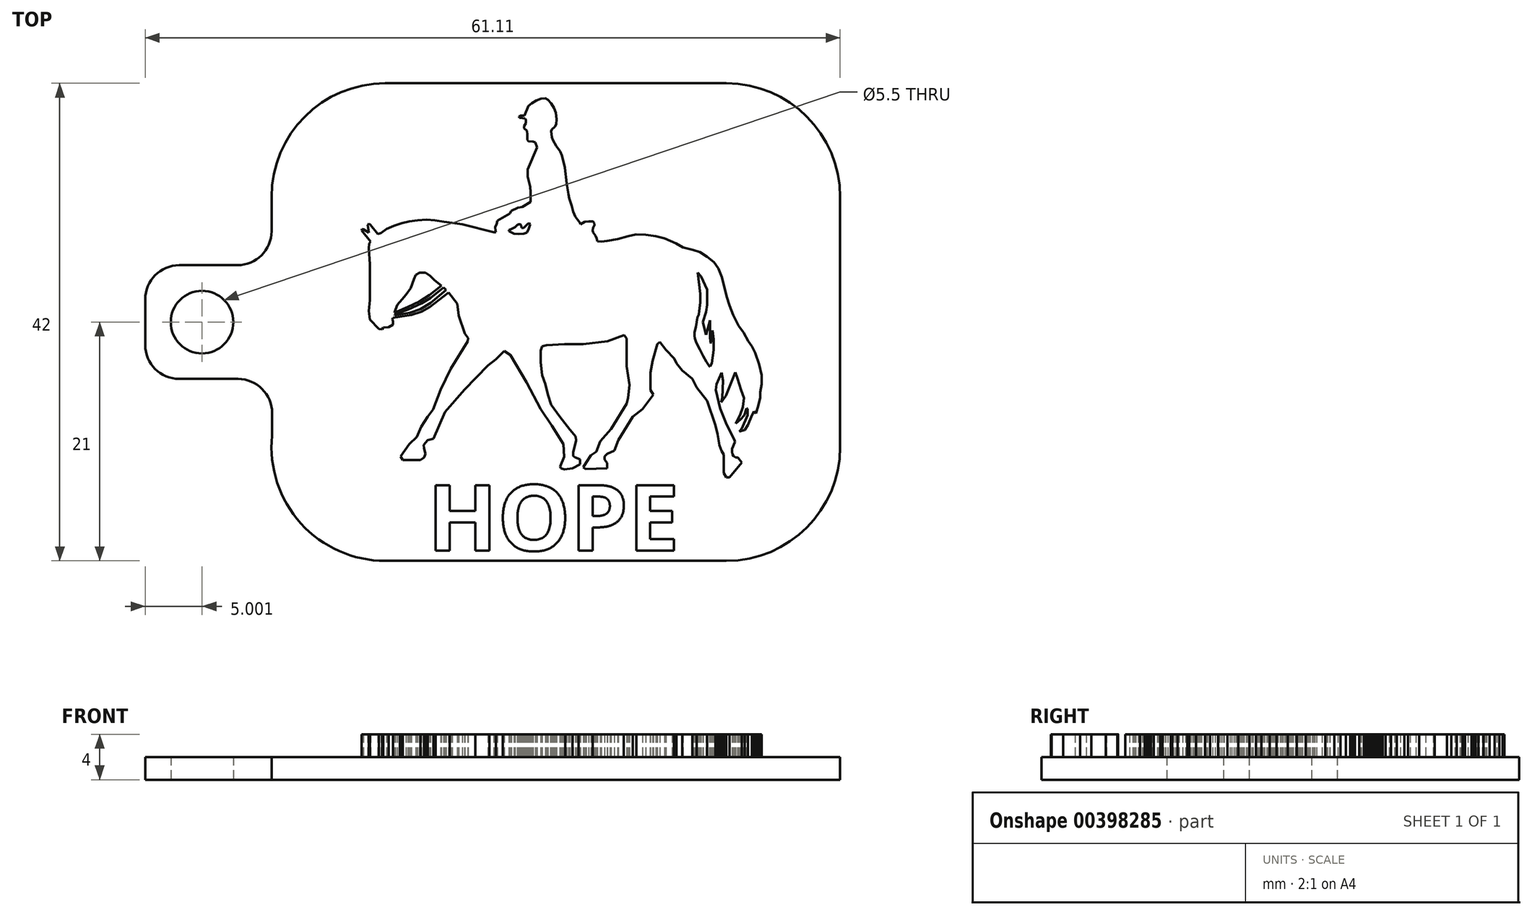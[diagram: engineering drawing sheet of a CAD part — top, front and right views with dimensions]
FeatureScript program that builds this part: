
annotation { "Feature Type Name" : "Feature", "Feature Type Description" : "" }
export const myFeature = defineFeature(function(context is Context, id is Id, definition is map)
    precondition{}
    {
        {
            var Q0;
            Q0=qCreatedBy(makeId("Top.planeOp"),FACE);
            var sketch = newSketch(context, id + "F0", { "sketchPlane" : qUnion([Q0])});
            skLineSegment(sketch, "E0.bottom", {"start": v(-3.2, -21) * mm, "end": v(26.8, -21) * mm});
            skLineSegment(sketch, "E0.top", {"start": v(-3.2, 21) * mm, "end": v(26.8, 21) * mm});
            skLineSegment(sketch, "E0.left", {"start": v(-13.2, 8) * mm, "end": v(-13.2, 11) * mm});
            skLineSegment(sketch, "E0.right", {"start": v(36.8, -11) * mm, "end": v(36.8, 11) * mm});
            skPoint(sketch, "E1.visualSharp", {"position": v(-13.2, 21) * mm});
            skArc(sketch, "E1.filletArc", {"start": v(-3.2, 21) * mm, "mid": v(-10.27, 18.07) * mm, "end": v(-13.2, 11) * mm});
            skPoint(sketch, "E2.visualSharp", {"position": v(36.8, 21) * mm});
            skArc(sketch, "E2.filletArc", {"start": v(36.8, 11) * mm, "mid": v(33.87, 18.07) * mm, "end": v(26.8, 21) * mm});
            skPoint(sketch, "E3.visualSharp", {"position": v(36.8, -21) * mm});
            skArc(sketch, "E3.filletArc", {"start": v(26.8, -21) * mm, "mid": v(33.87, -18.07) * mm, "end": v(36.8, -11) * mm});
            skPoint(sketch, "E4.visualSharp", {"position": v(-13.2, -21) * mm});
            skArc(sketch, "E4.filletArc", {"start": v(-13.15, -10) * mm, "mid": v(-10.62, -17.7) * mm, "end": v(-3.2, -21) * mm});
            skPoint(sketch, "E5.endSnap0", {"position": v(-13.2, 0) * mm});
            skLineSegment(sketch, "E6.0", {"start": v(-16.2, 5) * mm, "end": v(-21.3, 5) * mm});
            skLineSegment(sketch, "E7.0", {"start": v(-16.15, -5) * mm, "end": v(-21.3, -5) * mm});
            skLineSegment(sketch, "E8", {"start": v(-24.3, 2) * mm, "end": v(-24.3, -2) * mm});
            skPoint(sketch, "E9.visualSharp", {"position": v(-24.3, 5) * mm});
            skArc(sketch, "E9.filletArc", {"start": v(-21.3, 5) * mm, "mid": v(-23.43, 4.12) * mm, "end": v(-24.3, 2) * mm});
            skPoint(sketch, "E10.visualSharp", {"position": v(-24.3, -5) * mm});
            skArc(sketch, "E10.filletArc", {"start": v(-24.3, -2) * mm, "mid": v(-23.43, -4.12) * mm, "end": v(-21.3, -5) * mm});
            skPoint(sketch, "E11.centerSnap0", {"position": v(-24.3, 0) * mm});
            skPoint(sketch, "E12.newPointB", {"position": v(-13.2, -11) * mm});
            skArc(sketch, "E12.filletArc", {"start": v(-16.2, 5) * mm, "mid": v(-14.08, 5.88) * mm, "end": v(-13.2, 8) * mm});
            skLineSegment(sketch, "E13", {"start": v(-13.15, -10) * mm, "end": v(-13.15, -8) * mm});
            skPoint(sketch, "E14.visualSharp", {"position": v(-13.15, -5) * mm});
            skArc(sketch, "E14.filletArc", {"start": v(-13.15, -8) * mm, "mid": v(-14.03, -5.88) * mm, "end": v(-16.15, -5) * mm});
            skCircle(sketch, "E15", {"center": v(-19.3, 0) * mm, "radius": 2.75 * mm});
            skSolve(sketch);
        }
        {
            var Q0;
            Q0=makeQuery(id+"F0.imprint","IMPRINT",FACE,{"disambiguationData":[TD([[makeQuery(id+"F0.imprint","IMPRINT",EDGE,{"derivedFrom":sQuery(id+"F0.wireOp",EDGE,"E0.bottom")}),1.0]])]});
            extrude(context, id + "F1", {"entities" : qUnion([Q0]), "depth" : 2 * mm});
        }
        {
            var Q0;
            Q0=makeQuery(id+"F1.opExtrude","CAP_FACE",FACE,{"disambiguationData":[OSD([sQuery(id+"F0.wireOp",EDGE,"E0.bottom"),sQuery(id+"F0.wireOp",EDGE,"E0.top"),sQuery(id+"F0.wireOp",EDGE,"E0.left"),sQuery(id+"F0.wireOp",EDGE,"E0.right"),sQuery(id+"F0.wireOp",EDGE,"E1.filletArc"),sQuery(id+"F0.wireOp",EDGE,"E2.filletArc"),sQuery(id+"F0.wireOp",EDGE,"E3.filletArc"),sQuery(id+"F0.wireOp",EDGE,"E4.filletArc"),sQuery(id+"F0.wireOp",EDGE,"E6.0"),sQuery(id+"F0.wireOp",EDGE,"E7.0"),sQuery(id+"F0.wireOp",EDGE,"E8"),sQuery(id+"F0.wireOp",EDGE,"E9.filletArc"),sQuery(id+"F0.wireOp",EDGE,"E10.filletArc"),sQuery(id+"F0.wireOp",EDGE,"E12.filletArc"),sQuery(id+"F0.wireOp",EDGE,"E13"),sQuery(id+"F0.wireOp",EDGE,"E14.filletArc"),sQuery(id+"F0.wireOp",EDGE,"E15")])],"isStart":false});
            var sketch = newSketch(context, id + "F2", { "sketchPlane" : qUnion([Q0])});
            skLineSegment(sketch, "E16", {"start": v(16.3, -12.87) * mm, "end": v(14.4, -12.93) * mm});
            skLineSegment(sketch, "E17", {"start": v(14.4, -12.93) * mm, "end": v(14.2, -12.76) * mm});
            skLineSegment(sketch, "E18", {"start": v(14.2, -12.76) * mm, "end": v(14.47, -12.34) * mm});
            skLineSegment(sketch, "E19", {"start": v(14.47, -12.34) * mm, "end": v(14.89, -11.72) * mm});
            skLineSegment(sketch, "E20", {"start": v(14.89, -11.72) * mm, "end": v(15.37, -11.4) * mm});
            skLineSegment(sketch, "E21", {"start": v(15.37, -11.4) * mm, "end": v(15.72, -10.49) * mm});
            skLineSegment(sketch, "E22", {"start": v(15.72, -10.49) * mm, "end": v(16.66, -9.4) * mm});
            skLineSegment(sketch, "E23", {"start": v(16.66, -9.4) * mm, "end": v(18.04, -7.18) * mm});
            skLineSegment(sketch, "E24", {"start": v(18.04, -7.18) * mm, "end": v(18.15, -6.68) * mm});
            skLineSegment(sketch, "E25", {"start": v(18.15, -6.68) * mm, "end": v(18.28, -5.52) * mm});
            skLineSegment(sketch, "E26", {"start": v(18.28, -5.52) * mm, "end": v(18.04, -3.88) * mm});
            skLineSegment(sketch, "E27", {"start": v(18.04, -3.88) * mm, "end": v(18.04, -2.46) * mm});
            skLineSegment(sketch, "E28", {"start": v(18.04, -2.46) * mm, "end": v(18.04, -1.42) * mm});
            skLineSegment(sketch, "E29", {"start": v(18.04, -1.42) * mm, "end": v(17.82, -1.14) * mm});
            skLineSegment(sketch, "E30", {"start": v(17.82, -1.14) * mm, "end": v(16.33, -1.68) * mm});
            skLineSegment(sketch, "E31", {"start": v(16.33, -1.68) * mm, "end": v(14.22, -1.94) * mm});
            skLineSegment(sketch, "E32", {"start": v(14.22, -1.94) * mm, "end": v(12.55, -1.94) * mm});
            skLineSegment(sketch, "E33", {"start": v(12.55, -1.94) * mm, "end": v(10.97, -2.03) * mm});
            skLineSegment(sketch, "E34", {"start": v(10.97, -2.03) * mm, "end": v(10.59, -2.12) * mm});
            skLineSegment(sketch, "E35", {"start": v(10.59, -2.12) * mm, "end": v(10.47, -2.52) * mm});
            skLineSegment(sketch, "E36", {"start": v(10.47, -2.52) * mm, "end": v(10.47, -3.52) * mm});
            skLineSegment(sketch, "E37", {"start": v(10.47, -3.52) * mm, "end": v(10.6, -4.66) * mm});
            skLineSegment(sketch, "E38", {"start": v(10.6, -4.66) * mm, "end": v(10.88, -5.47) * mm});
            skLineSegment(sketch, "E39", {"start": v(10.88, -5.47) * mm, "end": v(11.1, -6.4) * mm});
            skLineSegment(sketch, "E40", {"start": v(11.1, -6.4) * mm, "end": v(11.39, -7.28) * mm});
            skLineSegment(sketch, "E41", {"start": v(11.39, -7.28) * mm, "end": v(12.15, -8.34) * mm});
            skLineSegment(sketch, "E42", {"start": v(12.15, -8.34) * mm, "end": v(13.04, -9.48) * mm});
            skLineSegment(sketch, "E43", {"start": v(13.04, -9.48) * mm, "end": v(13.55, -10.07) * mm});
            skLineSegment(sketch, "E44", {"start": v(13.55, -10.07) * mm, "end": v(13.6, -10.4) * mm});
            skLineSegment(sketch, "E45", {"start": v(13.6, -10.4) * mm, "end": v(13.33, -11.45) * mm});
            skLineSegment(sketch, "E46", {"start": v(13.33, -11.45) * mm, "end": v(13.33, -11.77) * mm});
            skLineSegment(sketch, "E47", {"start": v(13.33, -11.77) * mm, "end": v(13.52, -11.9) * mm});
            skLineSegment(sketch, "E48", {"start": v(13.52, -11.9) * mm, "end": v(13.92, -12.07) * mm});
            skLineSegment(sketch, "E49", {"start": v(13.92, -12.07) * mm, "end": v(13.92, -12.5) * mm});
            skLineSegment(sketch, "E50", {"start": v(13.92, -12.5) * mm, "end": v(13.27, -12.88) * mm});
            skLineSegment(sketch, "E51", {"start": v(13.27, -12.88) * mm, "end": v(12.55, -12.97) * mm});
            skLineSegment(sketch, "E52", {"start": v(12.55, -12.97) * mm, "end": v(12.25, -12.88) * mm});
            skLineSegment(sketch, "E53", {"start": v(12.25, -12.88) * mm, "end": v(12.19, -12.7) * mm});
            skLineSegment(sketch, "E54", {"start": v(12.19, -12.7) * mm, "end": v(12.54, -11.84) * mm});
            skLineSegment(sketch, "E55", {"start": v(12.54, -11.84) * mm, "end": v(12.46, -10.72) * mm});
            skLineSegment(sketch, "E56", {"start": v(12.46, -10.72) * mm, "end": v(11.44, -9.1) * mm});
            skLineSegment(sketch, "E57", {"start": v(11.44, -9.1) * mm, "end": v(10.47, -7.66) * mm});
            skLineSegment(sketch, "E58", {"start": v(10.47, -7.66) * mm, "end": v(9.22, -5.32) * mm});
            skLineSegment(sketch, "E59", {"start": v(9.22, -5.32) * mm, "end": v(7.82, -2.88) * mm});
            skLineSegment(sketch, "E60", {"start": v(7.82, -2.88) * mm, "end": v(7.25, -2.53) * mm});
            skLineSegment(sketch, "E61", {"start": v(7.25, -2.53) * mm, "end": v(6.53, -3.27) * mm});
            skLineSegment(sketch, "E62", {"start": v(6.53, -3.27) * mm, "end": v(5.84, -3.81) * mm});
            skLineSegment(sketch, "E63", {"start": v(5.84, -3.81) * mm, "end": v(3.76, -5.94) * mm});
            skLineSegment(sketch, "E64", {"start": v(3.76, -5.94) * mm, "end": v(2.06, -7.9) * mm});
            skLineSegment(sketch, "E65", {"start": v(2.06, -7.9) * mm, "end": v(1.04, -10.26) * mm});
            skLineSegment(sketch, "E66", {"start": v(1.04, -10.26) * mm, "end": v(0.54, -10.38) * mm});
            skLineSegment(sketch, "E67", {"start": v(0.54, -10.38) * mm, "end": v(0.19, -10.8) * mm});
            skLineSegment(sketch, "E68", {"start": v(0.19, -10.8) * mm, "end": v(0.23, -11.13) * mm});
            skLineSegment(sketch, "E69", {"start": v(0.23, -11.13) * mm, "end": v(0.34, -11.6) * mm});
            skLineSegment(sketch, "E70", {"start": v(0.34, -11.6) * mm, "end": v(0.2, -11.9) * mm});
            skLineSegment(sketch, "E71", {"start": v(0.2, -11.9) * mm, "end": v(-0.1, -12.14) * mm});
            skLineSegment(sketch, "E72", {"start": v(-0.1, -12.14) * mm, "end": v(-1.65, -12.14) * mm});
            skLineSegment(sketch, "E73", {"start": v(-1.65, -12.14) * mm, "end": v(-1.85, -11.8) * mm});
            skLineSegment(sketch, "E74", {"start": v(-1.85, -11.8) * mm, "end": v(-1.1, -10.72) * mm});
            skLineSegment(sketch, "E75", {"start": v(-1.1, -10.72) * mm, "end": v(-0.43, -10.1) * mm});
            skLineSegment(sketch, "E76", {"start": v(-0.43, -10.1) * mm, "end": v(-0.05, -9.22) * mm});
            skLineSegment(sketch, "E77", {"start": v(-0.05, -9.22) * mm, "end": v(0.54, -8.34) * mm});
            skLineSegment(sketch, "E78", {"start": v(0.54, -8.34) * mm, "end": v(1, -7.7) * mm});
            skLineSegment(sketch, "E79", {"start": v(1, -7.7) * mm, "end": v(1.68, -5.95) * mm});
            skLineSegment(sketch, "E80", {"start": v(1.68, -5.95) * mm, "end": v(2.57, -4.1) * mm});
            skLineSegment(sketch, "E81", {"start": v(2.57, -4.1) * mm, "end": v(4.06, -1.68) * mm});
            skLineSegment(sketch, "E82", {"start": v(4.06, -1.68) * mm, "end": v(4.1, -1.4) * mm});
            skLineSegment(sketch, "E83", {"start": v(4.1, -1.4) * mm, "end": v(3.8, -1.01) * mm});
            skLineSegment(sketch, "E84", {"start": v(3.8, -1.01) * mm, "end": v(3.26, 0.58) * mm});
            skLineSegment(sketch, "E85", {"start": v(3.26, 0.58) * mm, "end": v(3.13, 1.63) * mm});
            skLineSegment(sketch, "E86", {"start": v(3.13, 1.63) * mm, "end": v(2.36, 2.6) * mm});
            skLineSegment(sketch, "E87", {"start": v(2.36, 2.6) * mm, "end": v(0.71, 1.32) * mm});
            skLineSegment(sketch, "E88", {"start": v(0.71, 1.32) * mm, "end": v(0, 0.9) * mm});
            skLineSegment(sketch, "E89", {"start": v(0, 0.9) * mm, "end": v(-0.9, 0.65) * mm});
            skLineSegment(sketch, "E90", {"start": v(-0.9, 0.65) * mm, "end": v(-1.91, 0.46) * mm});
            skLineSegment(sketch, "E91", {"start": v(-1.91, 0.46) * mm, "end": v(-2.5, 0.39) * mm});
            skLineSegment(sketch, "E92", {"start": v(-2.5, 0.39) * mm, "end": v(-2.58, 0.23) * mm});
            skLineSegment(sketch, "E93", {"start": v(-2.58, 0.23) * mm, "end": v(-2.53, 0.1) * mm});
            skLineSegment(sketch, "E94", {"start": v(-2.53, 0.1) * mm, "end": v(-2.5, 0) * mm});
            skLineSegment(sketch, "E95", {"start": v(-2.5, 0) * mm, "end": v(-2.5, -0.21) * mm});
            skLineSegment(sketch, "E96", {"start": v(-2.5, -0.21) * mm, "end": v(-2.89, -0.43) * mm});
            skLineSegment(sketch, "E97", {"start": v(-2.89, -0.43) * mm, "end": v(-3.4, -0.5) * mm});
            skLineSegment(sketch, "E98", {"start": v(-3.4, -0.5) * mm, "end": v(-3.47, -0.63) * mm});
            skLineSegment(sketch, "E99", {"start": v(-3.47, -0.63) * mm, "end": v(-3.75, -0.6) * mm});
            skLineSegment(sketch, "E100", {"start": v(-3.75, -0.6) * mm, "end": v(-4.56, 0.22) * mm});
            skLineSegment(sketch, "E101", {"start": v(-4.56, 0.22) * mm, "end": v(-4.66, 1) * mm});
            skLineSegment(sketch, "E102", {"start": v(-4.66, 1) * mm, "end": v(-4.55, 1.94) * mm});
            skLineSegment(sketch, "E103", {"start": v(-4.55, 1.94) * mm, "end": v(-4.55, 3.1) * mm});
            skLineSegment(sketch, "E104", {"start": v(-4.55, 3.1) * mm, "end": v(-4.55, 5.06) * mm});
            skLineSegment(sketch, "E105", {"start": v(-4.55, 5.06) * mm, "end": v(-4.66, 6.47) * mm});
            skLineSegment(sketch, "E106", {"start": v(-4.66, 6.47) * mm, "end": v(-4.6, 6.9) * mm});
            skLineSegment(sketch, "E107", {"start": v(-4.6, 6.9) * mm, "end": v(-4.5, 7.08) * mm});
            skLineSegment(sketch, "E108", {"start": v(-4.5, 7.08) * mm, "end": v(-4.95, 7.66) * mm});
            skLineSegment(sketch, "E109", {"start": v(-4.95, 7.66) * mm, "end": v(-5.27, 8.07) * mm});
            skLineSegment(sketch, "E110", {"start": v(-5.27, 8.07) * mm, "end": v(-5.25, 8.17) * mm});
            skLineSegment(sketch, "E111", {"start": v(-5.25, 8.17) * mm, "end": v(-5.1, 8.16) * mm});
            skLineSegment(sketch, "E112", {"start": v(-5.1, 8.16) * mm, "end": v(-4.66, 7.88) * mm});
            skLineSegment(sketch, "E113", {"start": v(-4.66, 7.88) * mm, "end": v(-4.74, 8.53) * mm});
            skLineSegment(sketch, "E114", {"start": v(-4.74, 8.53) * mm, "end": v(-4.66, 8.67) * mm});
            skLineSegment(sketch, "E115", {"start": v(-4.66, 8.67) * mm, "end": v(-4.51, 8.58) * mm});
            skLineSegment(sketch, "E116", {"start": v(-4.51, 8.58) * mm, "end": v(-3.85, 7.74) * mm});
            skLineSegment(sketch, "E117", {"start": v(-3.85, 7.74) * mm, "end": v(-3.55, 7.84) * mm});
            skLineSegment(sketch, "E118", {"start": v(-3.55, 7.84) * mm, "end": v(-3.08, 8.17) * mm});
            skLineSegment(sketch, "E119", {"start": v(-3.08, 8.17) * mm, "end": v(-2.43, 8.47) * mm});
            skLineSegment(sketch, "E120", {"start": v(-2.43, 8.47) * mm, "end": v(-1.76, 8.7) * mm});
            skLineSegment(sketch, "E121", {"start": v(-1.76, 8.7) * mm, "end": v(-1.08, 8.85) * mm});
            skLineSegment(sketch, "E122", {"start": v(-1.08, 8.85) * mm, "end": v(-0.36, 8.94) * mm});
            skLineSegment(sketch, "E123", {"start": v(-0.36, 8.94) * mm, "end": v(0.44, 9) * mm});
            skLineSegment(sketch, "E124", {"start": v(0.44, 9) * mm, "end": v(1.15, 8.95) * mm});
            skLineSegment(sketch, "E125", {"start": v(1.15, 8.95) * mm, "end": v(1.95, 8.82) * mm});
            skLineSegment(sketch, "E126", {"start": v(1.95, 8.82) * mm, "end": v(2.68, 8.74) * mm});
            skLineSegment(sketch, "E127", {"start": v(2.68, 8.74) * mm, "end": v(3.57, 8.6) * mm});
            skLineSegment(sketch, "E128", {"start": v(3.57, 8.6) * mm, "end": v(4.4, 8.4) * mm});
            skLineSegment(sketch, "E129", {"start": v(4.4, 8.4) * mm, "end": v(5.28, 8.17) * mm});
            skLineSegment(sketch, "E130", {"start": v(5.28, 8.17) * mm, "end": v(6.34, 7.91) * mm});
            skLineSegment(sketch, "E131", {"start": v(6.34, 7.91) * mm, "end": v(6.53, 7.89) * mm});
            skLineSegment(sketch, "E132", {"start": v(6.53, 7.89) * mm, "end": v(6.5, 8) * mm});
            skLineSegment(sketch, "E133", {"start": v(6.5, 8) * mm, "end": v(6.45, 8.38) * mm});
            skLineSegment(sketch, "E134", {"start": v(6.45, 8.38) * mm, "end": v(6.59, 8.6) * mm});
            skLineSegment(sketch, "E135", {"start": v(6.59, 8.6) * mm, "end": v(6.67, 8.93) * mm});
            skLineSegment(sketch, "E136", {"start": v(6.67, 8.93) * mm, "end": v(7.17, 9.22) * mm});
            skLineSegment(sketch, "E137", {"start": v(7.17, 9.22) * mm, "end": v(7.77, 9.57) * mm});
            skLineSegment(sketch, "E138", {"start": v(7.77, 9.57) * mm, "end": v(7.86, 9.78) * mm});
            skLineSegment(sketch, "E139", {"start": v(7.86, 9.78) * mm, "end": v(8.47, 10.05) * mm});
            skLineSegment(sketch, "E140", {"start": v(8.47, 10.05) * mm, "end": v(8.84, 10.13) * mm});
            skLineSegment(sketch, "E141", {"start": v(8.84, 10.13) * mm, "end": v(9.6, 10.57) * mm});
            skLineSegment(sketch, "E142", {"start": v(9.6, 10.57) * mm, "end": v(9.6, 11.1) * mm});
            skLineSegment(sketch, "E143", {"start": v(9.6, 11.1) * mm, "end": v(9.6, 11.41) * mm});
            skLineSegment(sketch, "E144", {"start": v(9.6, 11.41) * mm, "end": v(9.53, 11.92) * mm});
            skLineSegment(sketch, "E145", {"start": v(9.53, 11.92) * mm, "end": v(9.33, 12.78) * mm});
            skLineSegment(sketch, "E146", {"start": v(9.33, 12.78) * mm, "end": v(9.33, 13.43) * mm});
            skLineSegment(sketch, "E147", {"start": v(9.33, 13.43) * mm, "end": v(9.92, 14.8) * mm});
            skLineSegment(sketch, "E148", {"start": v(9.92, 14.8) * mm, "end": v(10.16, 15.35) * mm});
            skLineSegment(sketch, "E149", {"start": v(10.16, 15.35) * mm, "end": v(9.98, 15.8) * mm});
            skLineSegment(sketch, "E150", {"start": v(9.98, 15.8) * mm, "end": v(9.81, 15.87) * mm});
            skLineSegment(sketch, "E151", {"start": v(9.81, 15.87) * mm, "end": v(9.4, 15.92) * mm});
            skLineSegment(sketch, "E152", {"start": v(9.4, 15.92) * mm, "end": v(9.3, 16.04) * mm});
            skLineSegment(sketch, "E153", {"start": v(9.3, 16.04) * mm, "end": v(9.3, 16.5) * mm});
            skLineSegment(sketch, "E154", {"start": v(9.3, 16.5) * mm, "end": v(9.25, 16.83) * mm});
            skLineSegment(sketch, "E155", {"start": v(9.25, 16.83) * mm, "end": v(9.02, 17.04) * mm});
            skLineSegment(sketch, "E156", {"start": v(9.02, 17.04) * mm, "end": v(9, 17.1) * mm});
            skLineSegment(sketch, "E157", {"start": v(9, 17.1) * mm, "end": v(9, 17.22) * mm});
            skLineSegment(sketch, "E158", {"start": v(9, 17.22) * mm, "end": v(9.17, 17.49) * mm});
            skLineSegment(sketch, "E159", {"start": v(9.17, 17.49) * mm, "end": v(9.17, 17.77) * mm});
            skLineSegment(sketch, "E160", {"start": v(9.17, 17.77) * mm, "end": v(9.12, 17.9) * mm});
            skLineSegment(sketch, "E161", {"start": v(9.12, 17.9) * mm, "end": v(8.88, 17.93) * mm});
            skLineSegment(sketch, "E162", {"start": v(8.88, 17.93) * mm, "end": v(8.6, 17.97) * mm});
            skLineSegment(sketch, "E163", {"start": v(8.6, 17.97) * mm, "end": v(8.58, 18.1) * mm});
            skLineSegment(sketch, "E164", {"start": v(8.58, 18.1) * mm, "end": v(8.67, 18.16) * mm});
            skLineSegment(sketch, "E165", {"start": v(8.67, 18.16) * mm, "end": v(9.03, 18.16) * mm});
            skLineSegment(sketch, "E166", {"start": v(9.03, 18.16) * mm, "end": v(9.4, 19.02) * mm});
            skLineSegment(sketch, "E167", {"start": v(9.4, 19.02) * mm, "end": v(9.69, 19.24) * mm});
            skLineSegment(sketch, "E168", {"start": v(9.69, 19.24) * mm, "end": v(10.1, 19.48) * mm});
            skLineSegment(sketch, "E169", {"start": v(10.1, 19.48) * mm, "end": v(10.5, 19.64) * mm});
            skLineSegment(sketch, "E170", {"start": v(10.5, 19.64) * mm, "end": v(10.88, 19.69) * mm});
            skLineSegment(sketch, "E171", {"start": v(10.88, 19.69) * mm, "end": v(11.1, 19.55) * mm});
            skLineSegment(sketch, "E172", {"start": v(11.1, 19.55) * mm, "end": v(11.39, 19.25) * mm});
            skLineSegment(sketch, "E173", {"start": v(11.39, 19.25) * mm, "end": v(11.63, 18.83) * mm});
            skLineSegment(sketch, "E174", {"start": v(11.63, 18.83) * mm, "end": v(11.8, 18.4) * mm});
            skLineSegment(sketch, "E175", {"start": v(11.8, 18.4) * mm, "end": v(11.87, 17.85) * mm});
            skLineSegment(sketch, "E176", {"start": v(11.87, 17.85) * mm, "end": v(11.82, 17.4) * mm});
            skLineSegment(sketch, "E177", {"start": v(11.82, 17.4) * mm, "end": v(11.72, 17.17) * mm});
            skLineSegment(sketch, "E178", {"start": v(11.72, 17.17) * mm, "end": v(11.46, 16.97) * mm});
            skLineSegment(sketch, "E179", {"start": v(11.46, 16.97) * mm, "end": v(11.39, 16.8) * mm});
            skLineSegment(sketch, "E180", {"start": v(11.39, 16.8) * mm, "end": v(11.4, 16.67) * mm});
            skLineSegment(sketch, "E181", {"start": v(11.4, 16.67) * mm, "end": v(11.43, 16.45) * mm});
            skLineSegment(sketch, "E182", {"start": v(11.43, 16.45) * mm, "end": v(11.46, 16.24) * mm});
            skLineSegment(sketch, "E183", {"start": v(11.46, 16.24) * mm, "end": v(11.55, 16) * mm});
            skLineSegment(sketch, "E184", {"start": v(11.55, 16) * mm, "end": v(11.84, 15.5) * mm});
            skLineSegment(sketch, "E185", {"start": v(11.84, 15.5) * mm, "end": v(12.18, 15.02) * mm});
            skLineSegment(sketch, "E186", {"start": v(12.18, 15.02) * mm, "end": v(12.34, 14.64) * mm});
            skLineSegment(sketch, "E187", {"start": v(12.34, 14.64) * mm, "end": v(12.46, 14.1) * mm});
            skLineSegment(sketch, "E188", {"start": v(12.46, 14.1) * mm, "end": v(12.58, 13.57) * mm});
            skLineSegment(sketch, "E189", {"start": v(12.58, 13.57) * mm, "end": v(12.64, 13.13) * mm});
            skLineSegment(sketch, "E190", {"start": v(12.64, 13.13) * mm, "end": v(12.7, 12.66) * mm});
            skLineSegment(sketch, "E191", {"start": v(12.7, 12.66) * mm, "end": v(12.75, 12.2) * mm});
            skLineSegment(sketch, "E192", {"start": v(12.75, 12.2) * mm, "end": v(12.92, 11.22) * mm});
            skLineSegment(sketch, "E193", {"start": v(12.92, 11.22) * mm, "end": v(12.96, 10.9) * mm});
            skLineSegment(sketch, "E194", {"start": v(12.96, 10.9) * mm, "end": v(13.19, 10.22) * mm});
            skLineSegment(sketch, "E195", {"start": v(13.19, 10.22) * mm, "end": v(13.33, 9.73) * mm});
            skLineSegment(sketch, "E196", {"start": v(13.33, 9.73) * mm, "end": v(13.52, 9.26) * mm});
            skLineSegment(sketch, "E197", {"start": v(13.52, 9.26) * mm, "end": v(13.72, 9) * mm});
            skLineSegment(sketch, "E198", {"start": v(13.72, 9) * mm, "end": v(13.92, 8.73) * mm});
            skLineSegment(sketch, "E199", {"start": v(13.92, 8.73) * mm, "end": v(13.96, 8.61) * mm});
            skLineSegment(sketch, "E200", {"start": v(13.96, 8.61) * mm, "end": v(14.35, 8.8) * mm});
            skLineSegment(sketch, "E201", {"start": v(14.35, 8.8) * mm, "end": v(14.68, 8.85) * mm});
            skLineSegment(sketch, "E202", {"start": v(14.68, 8.85) * mm, "end": v(15.06, 8.85) * mm});
            skLineSegment(sketch, "E203", {"start": v(15.06, 8.85) * mm, "end": v(15.16, 8.73) * mm});
            skLineSegment(sketch, "E204", {"start": v(15.16, 8.73) * mm, "end": v(15.19, 8.54) * mm});
            skLineSegment(sketch, "E205", {"start": v(15.19, 8.54) * mm, "end": v(15.09, 8.3) * mm});
            skLineSegment(sketch, "E206", {"start": v(15.09, 8.3) * mm, "end": v(15.03, 8.07) * mm});
            skLineSegment(sketch, "E207", {"start": v(15.03, 8.07) * mm, "end": v(15.08, 7.89) * mm});
            skLineSegment(sketch, "E208", {"start": v(15.08, 7.89) * mm, "end": v(15.29, 7.6) * mm});
            skLineSegment(sketch, "E209", {"start": v(15.29, 7.6) * mm, "end": v(15.38, 7.38) * mm});
            skLineSegment(sketch, "E210", {"start": v(15.38, 7.38) * mm, "end": v(15.45, 7.12) * mm});
            skLineSegment(sketch, "E211", {"start": v(15.45, 7.12) * mm, "end": v(15.8, 7.08) * mm});
            skLineSegment(sketch, "E212", {"start": v(15.8, 7.08) * mm, "end": v(16.31, 7.14) * mm});
            skLineSegment(sketch, "E213", {"start": v(16.31, 7.14) * mm, "end": v(17.24, 7.3) * mm});
            skLineSegment(sketch, "E214", {"start": v(17.24, 7.3) * mm, "end": v(18.14, 7.56) * mm});
            skLineSegment(sketch, "E215", {"start": v(18.14, 7.56) * mm, "end": v(18.84, 7.72) * mm});
            skLineSegment(sketch, "E216", {"start": v(18.84, 7.72) * mm, "end": v(19.72, 7.7) * mm});
            skLineSegment(sketch, "E217", {"start": v(19.72, 7.7) * mm, "end": v(20.58, 7.56) * mm});
            skLineSegment(sketch, "E218", {"start": v(20.58, 7.56) * mm, "end": v(21.37, 7.36) * mm});
            skLineSegment(sketch, "E219", {"start": v(21.37, 7.36) * mm, "end": v(22.38, 6.92) * mm});
            skLineSegment(sketch, "E220", {"start": v(22.38, 6.92) * mm, "end": v(22.98, 6.56) * mm});
            skLineSegment(sketch, "E221", {"start": v(22.98, 6.56) * mm, "end": v(23.85, 6.34) * mm});
            skLineSegment(sketch, "E222", {"start": v(23.85, 6.34) * mm, "end": v(24.48, 6.15) * mm});
            skLineSegment(sketch, "E223", {"start": v(24.48, 6.15) * mm, "end": v(25.12, 5.76) * mm});
            skLineSegment(sketch, "E224", {"start": v(25.12, 5.76) * mm, "end": v(25.7, 5.28) * mm});
            skLineSegment(sketch, "E225", {"start": v(25.7, 5.28) * mm, "end": v(26.1, 4.73) * mm});
            skLineSegment(sketch, "E226", {"start": v(26.1, 4.73) * mm, "end": v(26.42, 3.94) * mm});
            skLineSegment(sketch, "E227", {"start": v(26.42, 3.94) * mm, "end": v(26.6, 3.18) * mm});
            skLineSegment(sketch, "E228", {"start": v(26.6, 3.18) * mm, "end": v(26.8, 2.24) * mm});
            skLineSegment(sketch, "E229", {"start": v(26.8, 2.24) * mm, "end": v(27.07, 1.45) * mm});
            skLineSegment(sketch, "E230", {"start": v(27.07, 1.45) * mm, "end": v(27.4, 0.65) * mm});
            skLineSegment(sketch, "E231", {"start": v(27.4, 0.65) * mm, "end": v(27.86, -0.32) * mm});
            skLineSegment(sketch, "E232", {"start": v(27.86, -0.32) * mm, "end": v(28.3, -0.93) * mm});
            skLineSegment(sketch, "E233", {"start": v(28.3, -0.93) * mm, "end": v(28.73, -1.68) * mm});
            skLineSegment(sketch, "E234", {"start": v(28.73, -1.68) * mm, "end": v(29.04, -2.13) * mm});
            skLineSegment(sketch, "E235", {"start": v(29.04, -2.13) * mm, "end": v(29.33, -2.7) * mm});
            skLineSegment(sketch, "E236", {"start": v(29.33, -2.7) * mm, "end": v(29.67, -3.7) * mm});
            skLineSegment(sketch, "E237", {"start": v(29.67, -3.7) * mm, "end": v(29.89, -4.66) * mm});
            skLineSegment(sketch, "E238", {"start": v(29.89, -4.66) * mm, "end": v(29.89, -5.47) * mm});
            skLineSegment(sketch, "E239", {"start": v(29.89, -5.47) * mm, "end": v(29.78, -6.17) * mm});
            skLineSegment(sketch, "E240", {"start": v(29.78, -6.17) * mm, "end": v(29.78, -6.63) * mm});
            skLineSegment(sketch, "E241", {"start": v(29.78, -6.63) * mm, "end": v(29.59, -7.42) * mm});
            skLineSegment(sketch, "E242", {"start": v(29.59, -7.42) * mm, "end": v(29.4, -8.02) * mm});
            skLineSegment(sketch, "E243", {"start": v(29.4, -8.02) * mm, "end": v(29.23, -7.85) * mm});
            skLineSegment(sketch, "E244", {"start": v(29.23, -7.85) * mm, "end": v(29.05, -8.19) * mm});
            skLineSegment(sketch, "E245", {"start": v(29.05, -8.19) * mm, "end": v(28.68, -9.04) * mm});
            skLineSegment(sketch, "E246", {"start": v(28.68, -9.04) * mm, "end": v(28.4, -9.5) * mm});
            skLineSegment(sketch, "E247", {"start": v(28.4, -9.5) * mm, "end": v(27.92, -9.62) * mm});
            skLineSegment(sketch, "E248", {"start": v(27.92, -9.62) * mm, "end": v(28.14, -9.37) * mm});
            skLineSegment(sketch, "E249", {"start": v(28.14, -9.37) * mm, "end": v(28.65, -8.19) * mm});
            skLineSegment(sketch, "E250", {"start": v(28.65, -8.19) * mm, "end": v(28.65, -7.61) * mm});
            skLineSegment(sketch, "E251", {"start": v(28.65, -7.61) * mm, "end": v(28.55, -7.6) * mm});
            skLineSegment(sketch, "E252", {"start": v(28.55, -7.6) * mm, "end": v(28.38, -8.19) * mm});
            skLineSegment(sketch, "E253", {"start": v(28.38, -8.19) * mm, "end": v(28.03, -8.58) * mm});
            skLineSegment(sketch, "E254", {"start": v(28.03, -8.58) * mm, "end": v(27.6, -8.92) * mm});
            skLineSegment(sketch, "E255", {"start": v(27.6, -8.92) * mm, "end": v(28, -8.19) * mm});
            skLineSegment(sketch, "E256", {"start": v(28, -8.19) * mm, "end": v(28.24, -7.48) * mm});
            skLineSegment(sketch, "E257", {"start": v(28.24, -7.48) * mm, "end": v(28.33, -6.66) * mm});
            skLineSegment(sketch, "E258", {"start": v(28.33, -6.66) * mm, "end": v(28.08, -5.96) * mm});
            skLineSegment(sketch, "E259", {"start": v(28.08, -5.96) * mm, "end": v(27.78, -4.95) * mm});
            skLineSegment(sketch, "E260", {"start": v(27.78, -4.95) * mm, "end": v(27.59, -4.43) * mm});
            skLineSegment(sketch, "E261", {"start": v(27.59, -4.43) * mm, "end": v(26.74, -6.47) * mm});
            skLineSegment(sketch, "E262", {"start": v(26.74, -6.47) * mm, "end": v(26.35, -7.06) * mm});
            skLineSegment(sketch, "E263", {"start": v(26.35, -7.06) * mm, "end": v(26.44, -6.63) * mm});
            skLineSegment(sketch, "E264", {"start": v(26.44, -6.63) * mm, "end": v(26.5, -5.16) * mm});
            skLineSegment(sketch, "E265", {"start": v(26.5, -5.16) * mm, "end": v(26.39, -4.44) * mm});
            skLineSegment(sketch, "E266", {"start": v(26.39, -4.44) * mm, "end": v(25.94, -5.47) * mm});
            skLineSegment(sketch, "E267", {"start": v(25.94, -5.47) * mm, "end": v(25.88, -5.96) * mm});
            skLineSegment(sketch, "E268", {"start": v(25.88, -5.96) * mm, "end": v(26.06, -6.74) * mm});
            skLineSegment(sketch, "E269", {"start": v(26.06, -6.74) * mm, "end": v(26.26, -7.6) * mm});
            skLineSegment(sketch, "E270", {"start": v(26.26, -7.6) * mm, "end": v(26.83, -9.03) * mm});
            skLineSegment(sketch, "E271", {"start": v(26.83, -9.03) * mm, "end": v(27.51, -10.38) * mm});
            skLineSegment(sketch, "E272", {"start": v(27.51, -10.38) * mm, "end": v(27.54, -10.55) * mm});
            skLineSegment(sketch, "E273", {"start": v(27.54, -10.55) * mm, "end": v(27.29, -11.13) * mm});
            skLineSegment(sketch, "E274", {"start": v(27.29, -11.13) * mm, "end": v(27.29, -11.4) * mm});
            skLineSegment(sketch, "E275", {"start": v(27.29, -11.4) * mm, "end": v(27.34, -11.62) * mm});
            skLineSegment(sketch, "E276", {"start": v(27.34, -11.62) * mm, "end": v(27.42, -11.77) * mm});
            skLineSegment(sketch, "E277", {"start": v(27.42, -11.77) * mm, "end": v(27.62, -11.9) * mm});
            skLineSegment(sketch, "E278", {"start": v(27.62, -11.9) * mm, "end": v(27.82, -11.91) * mm});
            skLineSegment(sketch, "E279", {"start": v(27.82, -11.91) * mm, "end": v(28.15, -12.34) * mm});
            skLineSegment(sketch, "E280", {"start": v(28.15, -12.34) * mm, "end": v(27.07, -13.65) * mm});
            skLineSegment(sketch, "E281", {"start": v(27.07, -13.65) * mm, "end": v(26.8, -13.65) * mm});
            skLineSegment(sketch, "E282", {"start": v(26.8, -13.65) * mm, "end": v(26.57, -13.27) * mm});
            skLineSegment(sketch, "E283", {"start": v(26.57, -13.27) * mm, "end": v(26.57, -11.65) * mm});
            skLineSegment(sketch, "E284", {"start": v(26.57, -11.65) * mm, "end": v(26.39, -11.34) * mm});
            skLineSegment(sketch, "E285", {"start": v(26.39, -11.34) * mm, "end": v(26.18, -10.82) * mm});
            skLineSegment(sketch, "E286", {"start": v(26.18, -10.82) * mm, "end": v(26.02, -9.9) * mm});
            skLineSegment(sketch, "E287", {"start": v(26.02, -9.9) * mm, "end": v(25.84, -9.1) * mm});
            skLineSegment(sketch, "E288", {"start": v(25.84, -9.1) * mm, "end": v(25.5, -8.1) * mm});
            skLineSegment(sketch, "E289", {"start": v(25.5, -8.1) * mm, "end": v(25.12, -6.94) * mm});
            skLineSegment(sketch, "E290", {"start": v(25.12, -6.94) * mm, "end": v(24.17, -5.74) * mm});
            skLineSegment(sketch, "E291", {"start": v(24.17, -5.74) * mm, "end": v(23.8, -5) * mm});
            skLineSegment(sketch, "E292", {"start": v(23.8, -5) * mm, "end": v(22.92, -4.27) * mm});
            skLineSegment(sketch, "E293", {"start": v(22.92, -4.27) * mm, "end": v(22.42, -3.63) * mm});
            skLineSegment(sketch, "E294", {"start": v(22.42, -3.63) * mm, "end": v(22.2, -3.2) * mm});
            skLineSegment(sketch, "E295", {"start": v(22.2, -3.2) * mm, "end": v(21.47, -2.44) * mm});
            skLineSegment(sketch, "E296", {"start": v(21.47, -2.44) * mm, "end": v(20.94, -1.76) * mm});
            skLineSegment(sketch, "E297", {"start": v(20.94, -1.76) * mm, "end": v(20.73, -1.93) * mm});
            skLineSegment(sketch, "E298", {"start": v(20.73, -1.93) * mm, "end": v(20.3, -3.4) * mm});
            skLineSegment(sketch, "E299", {"start": v(20.3, -3.4) * mm, "end": v(20.13, -4.44) * mm});
            skLineSegment(sketch, "E300", {"start": v(20.13, -4.44) * mm, "end": v(20.13, -5.96) * mm});
            skLineSegment(sketch, "E301", {"start": v(20.13, -5.96) * mm, "end": v(20.38, -6.4) * mm});
            skLineSegment(sketch, "E302", {"start": v(20.38, -6.4) * mm, "end": v(19.42, -7.67) * mm});
            skLineSegment(sketch, "E303", {"start": v(19.42, -7.67) * mm, "end": v(18.57, -8.34) * mm});
            skLineSegment(sketch, "E304", {"start": v(18.57, -8.34) * mm, "end": v(17.3, -10.38) * mm});
            skLineSegment(sketch, "E305", {"start": v(17.3, -10.38) * mm, "end": v(16.94, -11.3) * mm});
            skLineSegment(sketch, "E306", {"start": v(16.94, -11.3) * mm, "end": v(16.3, -11.6) * mm});
            skLineSegment(sketch, "E307", {"start": v(16.3, -11.6) * mm, "end": v(16.08, -11.81) * mm});
            skLineSegment(sketch, "E308", {"start": v(16.08, -11.81) * mm, "end": v(16.08, -12.1) * mm});
            skLineSegment(sketch, "E309", {"start": v(16.08, -12.1) * mm, "end": v(16.3, -12.4) * mm});
            skLineSegment(sketch, "E310", {"start": v(16.3, -12.4) * mm, "end": v(16.3, -12.87) * mm});
            skLineSegment(sketch, "E311", {"start": v(7.67, 7.98) * mm, "end": v(8.12, 7.8) * mm});
            skLineSegment(sketch, "E312", {"start": v(8.12, 7.8) * mm, "end": v(8.53, 7.75) * mm});
            skLineSegment(sketch, "E313", {"start": v(8.53, 7.75) * mm, "end": v(8.98, 7.77) * mm});
            skLineSegment(sketch, "E314", {"start": v(8.98, 7.77) * mm, "end": v(9.26, 7.86) * mm});
            skLineSegment(sketch, "E315", {"start": v(9.26, 7.86) * mm, "end": v(9.43, 8.23) * mm});
            skLineSegment(sketch, "E316", {"start": v(9.43, 8.23) * mm, "end": v(9.53, 8.6) * mm});
            skLineSegment(sketch, "E317", {"start": v(9.53, 8.6) * mm, "end": v(9.5, 8.7) * mm});
            skLineSegment(sketch, "E318", {"start": v(9.5, 8.7) * mm, "end": v(9.34, 8.65) * mm});
            skLineSegment(sketch, "E319", {"start": v(9.34, 8.65) * mm, "end": v(8.97, 8.3) * mm});
            skLineSegment(sketch, "E320", {"start": v(8.97, 8.3) * mm, "end": v(8.79, 8.28) * mm});
            skLineSegment(sketch, "E321", {"start": v(8.79, 8.28) * mm, "end": v(8.74, 8.5) * mm});
            skLineSegment(sketch, "E322", {"start": v(8.74, 8.5) * mm, "end": v(8.69, 8.6) * mm});
            skLineSegment(sketch, "E323", {"start": v(8.69, 8.6) * mm, "end": v(8.52, 8.6) * mm});
            skLineSegment(sketch, "E324", {"start": v(8.52, 8.6) * mm, "end": v(8.4, 8.52) * mm});
            skLineSegment(sketch, "E325", {"start": v(8.4, 8.52) * mm, "end": v(8.2, 8.36) * mm});
            skLineSegment(sketch, "E326", {"start": v(8.2, 8.36) * mm, "end": v(7.9, 8.17) * mm});
            skLineSegment(sketch, "E327", {"start": v(7.9, 8.17) * mm, "end": v(7.69, 8.1) * mm});
            skLineSegment(sketch, "E328", {"start": v(7.69, 8.1) * mm, "end": v(7.67, 7.98) * mm});
            skLineSegment(sketch, "E329", {"start": v(1.74, 3.2) * mm, "end": v(1.14, 3.67) * mm});
            skLineSegment(sketch, "E330", {"start": v(1.14, 3.67) * mm, "end": v(0.75, 4.07) * mm});
            skLineSegment(sketch, "E331", {"start": v(0.75, 4.07) * mm, "end": v(0.33, 4.36) * mm});
            skLineSegment(sketch, "E332", {"start": v(0.33, 4.36) * mm, "end": v(-0.17, 4.36) * mm});
            skLineSegment(sketch, "E333", {"start": v(-0.17, 4.36) * mm, "end": v(-0.53, 4.16) * mm});
            skLineSegment(sketch, "E334", {"start": v(-0.53, 4.16) * mm, "end": v(-0.68, 3.77) * mm});
            skLineSegment(sketch, "E335", {"start": v(-0.68, 3.77) * mm, "end": v(-0.96, 2.97) * mm});
            skLineSegment(sketch, "E336", {"start": v(-0.96, 2.97) * mm, "end": v(-1.37, 2.4) * mm});
            skLineSegment(sketch, "E337", {"start": v(-1.37, 2.4) * mm, "end": v(-1.73, 2) * mm});
            skLineSegment(sketch, "E338", {"start": v(-1.73, 2) * mm, "end": v(-2.15, 1.51) * mm});
            skLineSegment(sketch, "E339", {"start": v(-2.15, 1.51) * mm, "end": v(-2.3, 1.11) * mm});
            skLineSegment(sketch, "E340", {"start": v(-2.3, 1.11) * mm, "end": v(-2.38, 0.84) * mm});
            skLineSegment(sketch, "E341", {"start": v(-2.38, 0.84) * mm, "end": v(-1.22, 1.33) * mm});
            skLineSegment(sketch, "E342", {"start": v(-1.22, 1.33) * mm, "end": v(-0.18, 1.82) * mm});
            skLineSegment(sketch, "E343", {"start": v(-0.18, 1.82) * mm, "end": v(0.68, 2.38) * mm});
            skLineSegment(sketch, "E344", {"start": v(0.68, 2.38) * mm, "end": v(1.74, 3.2) * mm});
            skLineSegment(sketch, "E345", {"start": v(1.92, 3.03) * mm, "end": v(0.78, 2.14) * mm});
            skLineSegment(sketch, "E346", {"start": v(0.78, 2.14) * mm, "end": v(0, 1.66) * mm});
            skLineSegment(sketch, "E347", {"start": v(0, 1.66) * mm, "end": v(-1.2, 1.1) * mm});
            skLineSegment(sketch, "E348", {"start": v(-1.2, 1.1) * mm, "end": v(-2.4, 0.67) * mm});
            skLineSegment(sketch, "E349", {"start": v(-2.4, 0.67) * mm, "end": v(-2.35, 0.61) * mm});
            skLineSegment(sketch, "E350", {"start": v(-2.35, 0.61) * mm, "end": v(-1.02, 0.82) * mm});
            skLineSegment(sketch, "E351", {"start": v(-1.02, 0.82) * mm, "end": v(-0.09, 1.14) * mm});
            skLineSegment(sketch, "E352", {"start": v(-0.09, 1.14) * mm, "end": v(0.78, 1.68) * mm});
            skLineSegment(sketch, "E353", {"start": v(0.78, 1.68) * mm, "end": v(2.14, 2.82) * mm});
            skLineSegment(sketch, "E354", {"start": v(2.14, 2.82) * mm, "end": v(1.92, 3.03) * mm});
            skLineSegment(sketch, "E355", {"start": v(24.29, 4.34) * mm, "end": v(24.4, 3.35) * mm});
            skLineSegment(sketch, "E356", {"start": v(24.4, 3.35) * mm, "end": v(24.52, 2.48) * mm});
            skLineSegment(sketch, "E357", {"start": v(24.52, 2.48) * mm, "end": v(24.52, 1.7) * mm});
            skLineSegment(sketch, "E358", {"start": v(24.52, 1.7) * mm, "end": v(24.4, 0.98) * mm});
            skLineSegment(sketch, "E359", {"start": v(24.4, 0.98) * mm, "end": v(24.36, 0.65) * mm});
            skLineSegment(sketch, "E360", {"start": v(24.36, 0.65) * mm, "end": v(24.24, 0.4) * mm});
            skLineSegment(sketch, "E361", {"start": v(24.24, 0.4) * mm, "end": v(24.13, -0.43) * mm});
            skLineSegment(sketch, "E362", {"start": v(24.13, -0.43) * mm, "end": v(23.98, -0.89) * mm});
            skLineSegment(sketch, "E363", {"start": v(23.98, -0.89) * mm, "end": v(23.98, -1.2) * mm});
            skLineSegment(sketch, "E364", {"start": v(23.98, -1.2) * mm, "end": v(24, -1.42) * mm});
            skLineSegment(sketch, "E365", {"start": v(24, -1.42) * mm, "end": v(24.16, -1.8) * mm});
            skLineSegment(sketch, "E366", {"start": v(24.16, -1.8) * mm, "end": v(24.47, -2.4) * mm});
            skLineSegment(sketch, "E367", {"start": v(24.47, -2.4) * mm, "end": v(24.77, -3) * mm});
            skLineSegment(sketch, "E368", {"start": v(24.77, -3) * mm, "end": v(25.05, -3.5) * mm});
            skLineSegment(sketch, "E369", {"start": v(25.05, -3.5) * mm, "end": v(25.28, -3.87) * mm});
            skLineSegment(sketch, "E370", {"start": v(25.28, -3.87) * mm, "end": v(25.37, -3.91) * mm});
            skLineSegment(sketch, "E371", {"start": v(25.37, -3.91) * mm, "end": v(25.5, -3.64) * mm});
            skLineSegment(sketch, "E372", {"start": v(25.5, -3.64) * mm, "end": v(25.67, -2.44) * mm});
            skLineSegment(sketch, "E373", {"start": v(25.67, -2.44) * mm, "end": v(25.67, -1.52) * mm});
            skLineSegment(sketch, "E374", {"start": v(25.67, -1.52) * mm, "end": v(25.57, -0.74) * mm});
            skLineSegment(sketch, "E375", {"start": v(25.57, -0.74) * mm, "end": v(25.42, -1.87) * mm});
            skLineSegment(sketch, "E376", {"start": v(25.42, -1.87) * mm, "end": v(25.36, -1.39) * mm});
            skLineSegment(sketch, "E377", {"start": v(25.36, -1.39) * mm, "end": v(25.36, 0.14) * mm});
            skLineSegment(sketch, "E378", {"start": v(25.36, 0.14) * mm, "end": v(25.02, -1.11) * mm});
            skLineSegment(sketch, "E379", {"start": v(25.02, -1.11) * mm, "end": v(24.74, 0) * mm});
            skLineSegment(sketch, "E380", {"start": v(24.74, 0) * mm, "end": v(25, 0.9) * mm});
            skLineSegment(sketch, "E381", {"start": v(25, 0.9) * mm, "end": v(25.1, 1.52) * mm});
            skLineSegment(sketch, "E382", {"start": v(25.1, 1.52) * mm, "end": v(25.1, 2.87) * mm});
            skLineSegment(sketch, "E383", {"start": v(25.1, 2.87) * mm, "end": v(24.57, 4.03) * mm});
            skLineSegment(sketch, "E384", {"start": v(24.57, 4.03) * mm, "end": v(24.29, 4.34) * mm});
            skSolve(sketch);
        }
        {
            var Q0;
            Q0=makeQuery(id+"F2.imprint","IMPRINT",FACE,{"disambiguationData":[TD([[makeQuery(id+"F2.imprint","IMPRINT",EDGE,{"derivedFrom":makeQuery(id+"F1.opExtrude","CAP_EDGE",EDGE,{"disambiguationData":[OSD([sQuery(id+"F0.wireOp",EDGE,"E0.bottom")])],"isStart":false})}),1.0]])]});
            var sketch = newSketch(context, id + "F3", { "sketchPlane" : qUnion([Q0])});
            skText(sketch, "E385", { "text": "HOPE", "fontName": "OpenSans-Bold.ttf"});
            const initialGuessF3  = {"E385": [0.00051, -0.0201, 1, 0, 0.0058]};
            skSetInitialGuess(sketch, initialGuessF3);
            skSolve(sketch);
        }
        {
            var Q0;
            Q0 = qSketchRegion(id + "F3", true);
            extrude(context, id + "F4", {"entities" : qUnion([Q0]), "operationType" : NewBodyOperationType.ADD, "depth" : 2 * mm});
        }
        {
            var Q0;
            Q0 = qSketchRegion(id + "F2", true);
            extrude(context, id + "F5", {"entities" : qUnion([Q0]), "operationType" : NewBodyOperationType.ADD, "depth" : 2 * mm});
        }
    });
